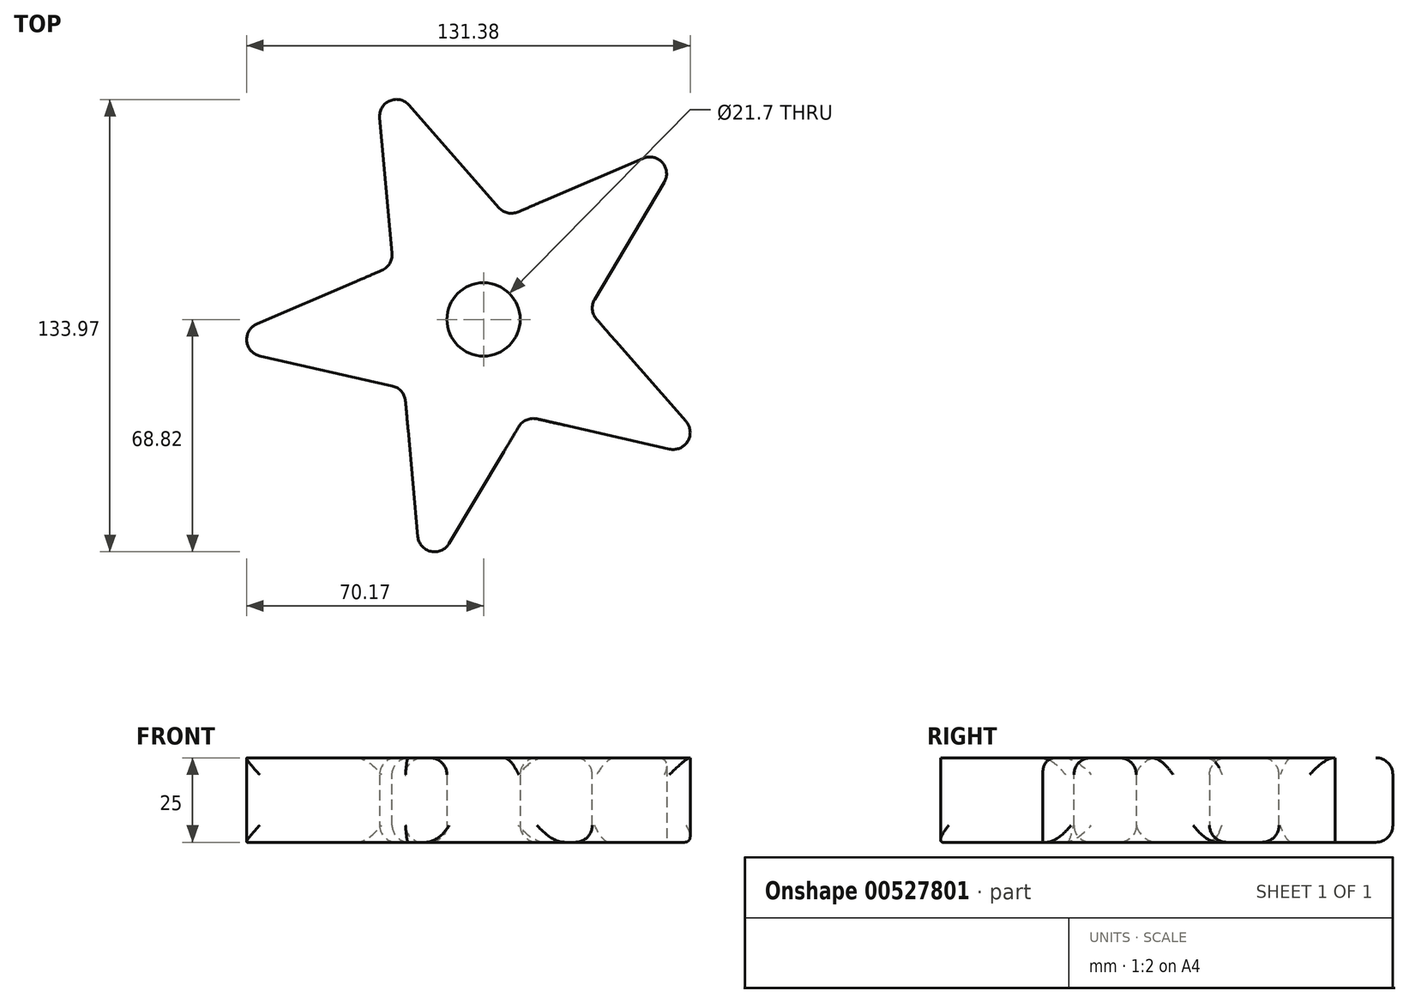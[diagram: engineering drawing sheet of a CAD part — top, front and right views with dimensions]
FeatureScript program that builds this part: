
annotation { "Feature Type Name" : "Feature", "Feature Type Description" : "" }
export const myFeature = defineFeature(function(context is Context, id is Id, definition is map)
    precondition{}
    {
        {
            var Q0;
            Q0=qCreatedBy(makeId("Top.planeOp"),FACE);
            var sketch = newSketch(context, id + "F0", { "sketchPlane" : qUnion([Q0])});
            skCircle(sketch, "E0.cCircle", {"center": v(0, 0) * mm, "radius": 25.22 * mm, "construction": true});
            skLineSegment(sketch, "E0.0", {"start": v(70.11, -41.8) * mm, "end": v(-81.29, -7.4) * mm});
            skLineSegment(sketch, "E0.1", {"start": v(-18.08, -79.6) * mm, "end": v(-32.16, 75.02) * mm});
            skLineSegment(sketch, "E0.2", {"start": v(-81.29, -7.4) * mm, "end": v(61.41, 53.77) * mm});
            skLineSegment(sketch, "E0.3", {"start": v(-32.16, 75.02) * mm, "end": v(70.11, -41.8) * mm});
            skLineSegment(sketch, "E0.4", {"start": v(61.41, 53.77) * mm, "end": v(-18.08, -79.6) * mm});
            skPoint(sketch, "E0.0.midPoint", {"position": v(-5.59, -24.6) * mm});
            skPoint(sketch, "E1.orphan", {"position": v(-23.46, -20.54) * mm});
            skPoint(sketch, "E2.orphan", {"position": v(-26.78, 15.96) * mm});
            skPoint(sketch, "E3.orphan", {"position": v(6.9, 30.4) * mm});
            skPoint(sketch, "E4.orphan", {"position": v(31.05, 2.83) * mm});
            skPoint(sketch, "E5.orphan", {"position": v(12.28, -28.66) * mm});
            skCircle(sketch, "E6", {"center": v(0, 0) * mm, "radius": 10.85 * mm});
            skSolve(sketch);
        }
        {
            var Q0;
            Q0 = qSketchRegion(id + "F0", true);
            extrude(context, id + "F1", {"entities" : qUnion([Q0]), "endBound" : BoundingType.SYMMETRIC, "depth" : 25 * mm, "offsetDistance" : 25 * mm});
        }
        {
            var Q0;
            Q0=makeQuery(id+"F1.opExtrude","SWEPT_EDGE",EDGE,{"disambiguationData":[OSD([sQuery(id+"F0.wireOp",EDGE,"E0.0"),sQuery(id+"F0.wireOp",EDGE,"E0.2")])]});
            var Q1;
            Q1=makeQuery(id+"F1.opExtrude","SWEPT_EDGE",EDGE,{"disambiguationData":[OSD([sQuery(id+"F0.wireOp",EDGE,"E0.0"),sQuery(id+"F0.wireOp",EDGE,"E0.1")])]});
            var Q2;
            Q2=makeQuery(id+"F1.opExtrude","SWEPT_EDGE",EDGE,{"disambiguationData":[OSD([sQuery(id+"F0.wireOp",EDGE,"E0.1"),sQuery(id+"F0.wireOp",EDGE,"E0.4")])]});
            var Q3;
            Q3=makeQuery(id+"F1.opExtrude","SWEPT_EDGE",EDGE,{"disambiguationData":[OSD([sQuery(id+"F0.wireOp",EDGE,"E0.0"),sQuery(id+"F0.wireOp",EDGE,"E0.4")])]});
            var Q4;
            Q4=makeQuery(id+"F1.opExtrude","SWEPT_EDGE",EDGE,{"disambiguationData":[OSD([sQuery(id+"F0.wireOp",EDGE,"E0.0"),sQuery(id+"F0.wireOp",EDGE,"E0.3")])]});
            var Q5;
            Q5=makeQuery(id+"F1.opExtrude","SWEPT_EDGE",EDGE,{"disambiguationData":[OSD([sQuery(id+"F0.wireOp",EDGE,"E0.3"),sQuery(id+"F0.wireOp",EDGE,"E0.4")])]});
            var Q6;
            Q6=makeQuery(id+"F1.opExtrude","SWEPT_EDGE",EDGE,{"disambiguationData":[OSD([sQuery(id+"F0.wireOp",EDGE,"E0.2"),sQuery(id+"F0.wireOp",EDGE,"E0.4")])]});
            var Q7;
            Q7=makeQuery(id+"F1.opExtrude","SWEPT_EDGE",EDGE,{"disambiguationData":[OSD([sQuery(id+"F0.wireOp",EDGE,"E0.2"),sQuery(id+"F0.wireOp",EDGE,"E0.3")])]});
            var Q8;
            Q8=makeQuery(id+"F1.opExtrude","SWEPT_EDGE",EDGE,{"disambiguationData":[OSD([sQuery(id+"F0.wireOp",EDGE,"E0.1"),sQuery(id+"F0.wireOp",EDGE,"E0.3")])]});
            var Q9;
            Q9=makeQuery(id+"F1.opExtrude","SWEPT_EDGE",EDGE,{"disambiguationData":[OSD([sQuery(id+"F0.wireOp",EDGE,"E0.1"),sQuery(id+"F0.wireOp",EDGE,"E0.2")])]});
            var Q10;
            {var subQ0=sQuery(id+"F0.wireOp",EDGE,"E0.1");Q10=makeQuery(id+"F1.opExtrude","CAP_EDGE",EDGE,{"disambiguationData":[OSD([subQ0]),TDD([makeQuery(id+"F0.imprint","IMPRINT",EDGE,{"disambiguationData":[TD([[makeQuery(id+"F0.imprint","INTERSECT",VERTEX,{"derivedFrom":[subQ0,sQuery(id+"F0.wireOp",EDGE,"E0.3")]}),1.0]])],"derivedFrom":subQ0})])],"isStart":false});}
            var Q11;
            {var subQ0=sQuery(id+"F0.wireOp",EDGE,"E0.3");Q11=makeQuery(id+"F1.opExtrude","CAP_EDGE",EDGE,{"disambiguationData":[OSD([subQ0]),TDD([makeQuery(id+"F0.imprint","IMPRINT",EDGE,{"disambiguationData":[TD([[makeQuery(id+"F0.imprint","INTERSECT",VERTEX,{"derivedFrom":[sQuery(id+"F0.wireOp",EDGE,"E0.1"),subQ0]}),-1.0]])],"derivedFrom":subQ0})])],"isStart":false});}
            var Q12;
            {var subQ0=sQuery(id+"F0.wireOp",EDGE,"E0.4");Q12=makeQuery(id+"F1.opExtrude","CAP_EDGE",EDGE,{"disambiguationData":[OSD([subQ0]),TDD([makeQuery(id+"F0.imprint","IMPRINT",EDGE,{"disambiguationData":[TD([[makeQuery(id+"F0.imprint","INTERSECT",VERTEX,{"derivedFrom":[sQuery(id+"F0.wireOp",EDGE,"E0.2"),subQ0]}),-1.0]])],"derivedFrom":subQ0})])],"isStart":false});}
            var Q13;
            {var subQ0=sQuery(id+"F0.wireOp",EDGE,"E0.0");Q13=makeQuery(id+"F1.opExtrude","CAP_EDGE",EDGE,{"disambiguationData":[OSD([subQ0]),TDD([makeQuery(id+"F0.imprint","IMPRINT",EDGE,{"disambiguationData":[TD([[makeQuery(id+"F0.imprint","INTERSECT",VERTEX,{"derivedFrom":[subQ0,sQuery(id+"F0.wireOp",EDGE,"E0.3")]}),-1.0]])],"derivedFrom":subQ0})])],"isStart":false});}
            var Q14;
            {var subQ0=sQuery(id+"F0.wireOp",EDGE,"E0.0");Q14=makeQuery(id+"F1.opExtrude","CAP_EDGE",EDGE,{"disambiguationData":[OSD([subQ0]),TDD([makeQuery(id+"F0.imprint","IMPRINT",EDGE,{"disambiguationData":[TD([[makeQuery(id+"F0.imprint","INTERSECT",VERTEX,{"derivedFrom":[subQ0,sQuery(id+"F0.wireOp",EDGE,"E0.2")]}),1.0]])],"derivedFrom":subQ0})])],"isStart":false});}
            var Q15;
            {var subQ0=sQuery(id+"F0.wireOp",EDGE,"E0.3");Q15=makeQuery(id+"F1.opExtrude","CAP_EDGE",EDGE,{"disambiguationData":[OSD([subQ0]),TDD([makeQuery(id+"F0.imprint","IMPRINT",EDGE,{"disambiguationData":[TD([[makeQuery(id+"F0.imprint","INTERSECT",VERTEX,{"derivedFrom":[sQuery(id+"F0.wireOp",EDGE,"E0.1"),subQ0]}),-1.0]])],"derivedFrom":subQ0})])],"isStart":true});}
            var Q16;
            {var subQ0=sQuery(id+"F0.wireOp",EDGE,"E0.1");Q16=makeQuery(id+"F1.opExtrude","CAP_EDGE",EDGE,{"disambiguationData":[OSD([subQ0]),TDD([makeQuery(id+"F0.imprint","IMPRINT",EDGE,{"disambiguationData":[TD([[makeQuery(id+"F0.imprint","INTERSECT",VERTEX,{"derivedFrom":[subQ0,sQuery(id+"F0.wireOp",EDGE,"E0.3")]}),1.0]])],"derivedFrom":subQ0})])],"isStart":true});}
            var Q17;
            {var subQ0=sQuery(id+"F0.wireOp",EDGE,"E0.0");Q17=makeQuery(id+"F1.opExtrude","CAP_EDGE",EDGE,{"disambiguationData":[OSD([subQ0]),TDD([makeQuery(id+"F0.imprint","IMPRINT",EDGE,{"disambiguationData":[TD([[makeQuery(id+"F0.imprint","INTERSECT",VERTEX,{"derivedFrom":[subQ0,sQuery(id+"F0.wireOp",EDGE,"E0.2")]}),1.0]])],"derivedFrom":subQ0})])],"isStart":true});}
            var Q18;
            {var subQ0=sQuery(id+"F0.wireOp",EDGE,"E0.4");Q18=makeQuery(id+"F1.opExtrude","CAP_EDGE",EDGE,{"disambiguationData":[OSD([subQ0]),TDD([makeQuery(id+"F0.imprint","IMPRINT",EDGE,{"disambiguationData":[TD([[makeQuery(id+"F0.imprint","INTERSECT",VERTEX,{"derivedFrom":[sQuery(id+"F0.wireOp",EDGE,"E0.1"),subQ0]}),1.0]])],"derivedFrom":subQ0})])],"isStart":true});}
            var Q19;
            {var subQ0=sQuery(id+"F0.wireOp",EDGE,"E0.3");Q19=makeQuery(id+"F1.opExtrude","CAP_EDGE",EDGE,{"disambiguationData":[OSD([subQ0]),TDD([makeQuery(id+"F0.imprint","IMPRINT",EDGE,{"disambiguationData":[TD([[makeQuery(id+"F0.imprint","INTERSECT",VERTEX,{"derivedFrom":[sQuery(id+"F0.wireOp",EDGE,"E0.0"),subQ0]}),1.0]])],"derivedFrom":subQ0})])],"isStart":true});}
            var Q20;
            Q20=makeQuery(id+"F1.opExtrude","CAP_EDGE",EDGE,{"disambiguationData":[OSD([sQuery(id+"F0.wireOp",EDGE,"E6")])],"isStart":false});
            var Q21;
            Q21=makeQuery(id+"F1.opExtrude","CAP_EDGE",EDGE,{"disambiguationData":[OSD([sQuery(id+"F0.wireOp",EDGE,"E6")])],"isStart":true});
            fillet(context, id + "F2", {"entities" : qUnion([Q0, Q1, Q2, Q3, Q4, Q5, Q6, Q7, Q8, Q9, Q10, Q11, Q12, Q13, Q14, Q15, Q16, Q17, Q18, Q19, Q20, Q21]), "radius" : 5 * mm, "tangentPropagation" : true, "allowEdgeOverflow" : false});
        }
    });
